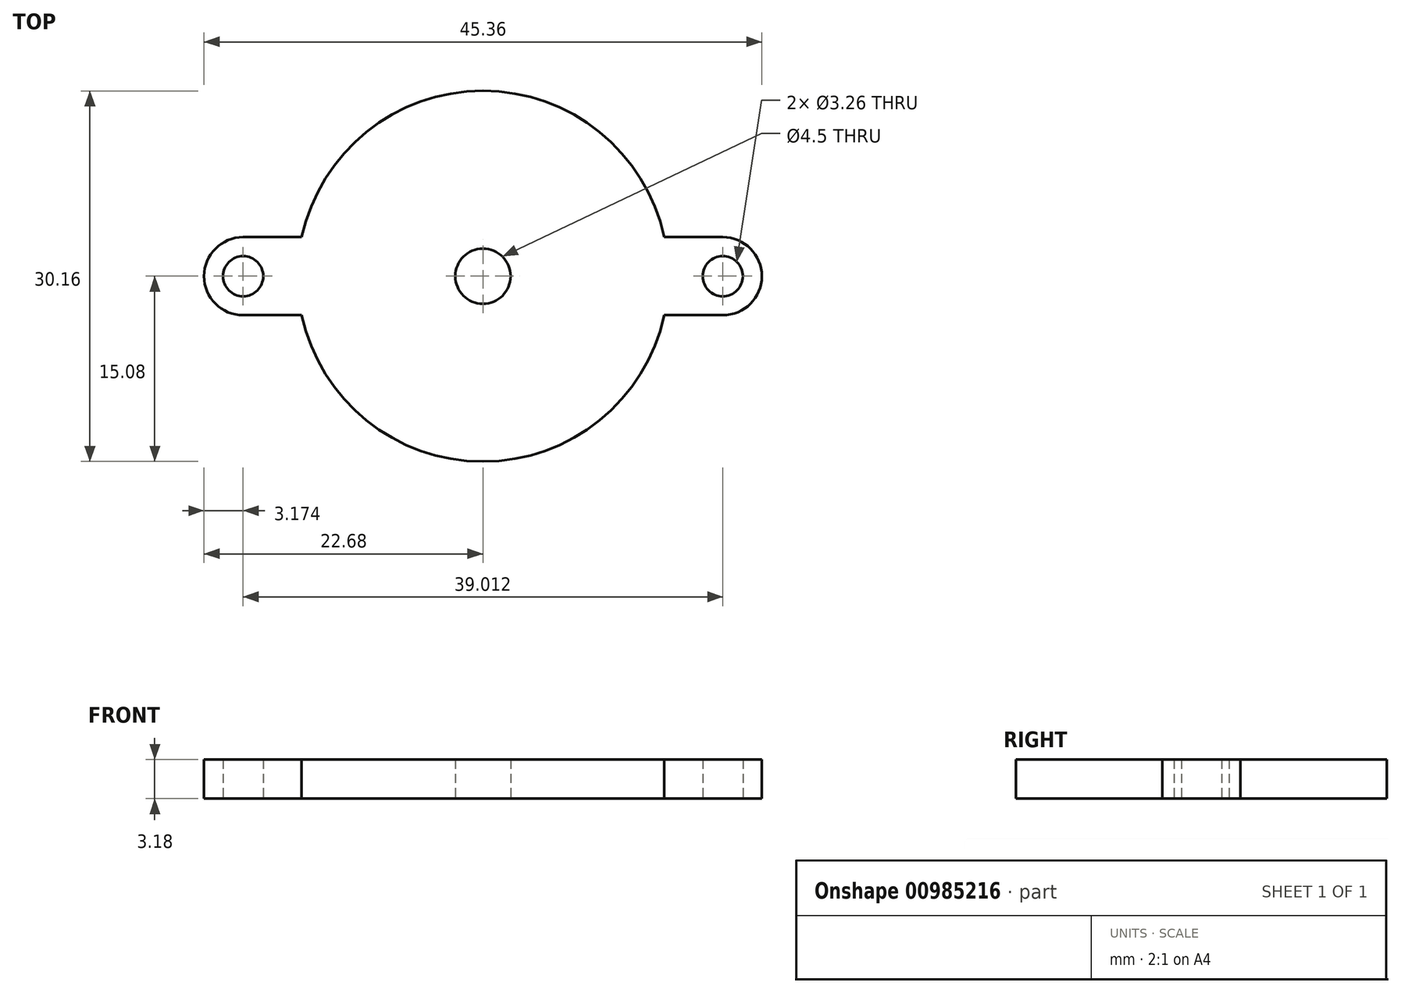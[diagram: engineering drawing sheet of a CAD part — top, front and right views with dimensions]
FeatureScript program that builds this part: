
annotation { "Feature Type Name" : "Feature", "Feature Type Description" : "" }
export const myFeature = defineFeature(function(context is Context, id is Id, definition is map)
    precondition{}
    {
        {
            var Q0;
            Q0=qCreatedBy(makeId("Top.planeOp"),FACE);
            var sketch = newSketch(context, id + "F0", { "sketchPlane" : qUnion([Q0])});
            skArc(sketch, "E0", {"start": v(14.74, 3.17) * mm, "mid": v(0, 15.08) * mm, "end": v(-14.74, 3.17) * mm});
            skCircle(sketch, "E1", {"center": v(0, 0) * mm, "radius": 2.25 * mm});
            skLineSegment(sketch, "E2.bottom", {"start": v(14.74, 3.18) * mm, "end": v(19.5, 3.18) * mm});
            skLineSegment(sketch, "E2.top", {"start": v(14.74, -3.18) * mm, "end": v(19.5, -3.18) * mm});
            skCircle(sketch, "E3", {"center": v(19.5, 0) * mm, "radius": 1.63 * mm});
            skArc(sketch, "E4", {"start": v(19.5, -3.18) * mm, "mid": v(22.68, 0) * mm, "end": v(19.5, 3.18) * mm});
            skLineSegment(sketch, "E5", {"start": v(0, 21.54) * mm, "end": v(0, -24) * mm, "construction": true});
            skLineSegment(sketch, "E6.MirrorCS", {"start": v(-14.74, 3.18) * mm, "end": v(-19.5, 3.18) * mm});
            skCircle(sketch, "E7.MirrorC", {"center": v(-19.5, 0) * mm, "radius": 1.63 * mm});
            skArc(sketch, "E8.MirrorCS", {"start": v(-19.5, -3.18) * mm, "mid": v(-22.68, 0) * mm, "end": v(-19.5, 3.18) * mm});
            skLineSegment(sketch, "E9.MirrorCS", {"start": v(-14.74, -3.18) * mm, "end": v(-19.5, -3.18) * mm});
            skArc(sketch, "E10.trimOffspring", {"start": v(-14.74, -3.17) * mm, "mid": v(0, -15.08) * mm, "end": v(14.74, -3.17) * mm});
            skSolve(sketch);
        }
        {
            var Q0;
            Q0 = qSketchRegion(id + "F0", true);
            extrude(context, id + "F1", {"entities" : qUnion([Q0]), "depth" : 3.17 * mm, "offsetDistance" : 25.4 * mm});
        }
    });
